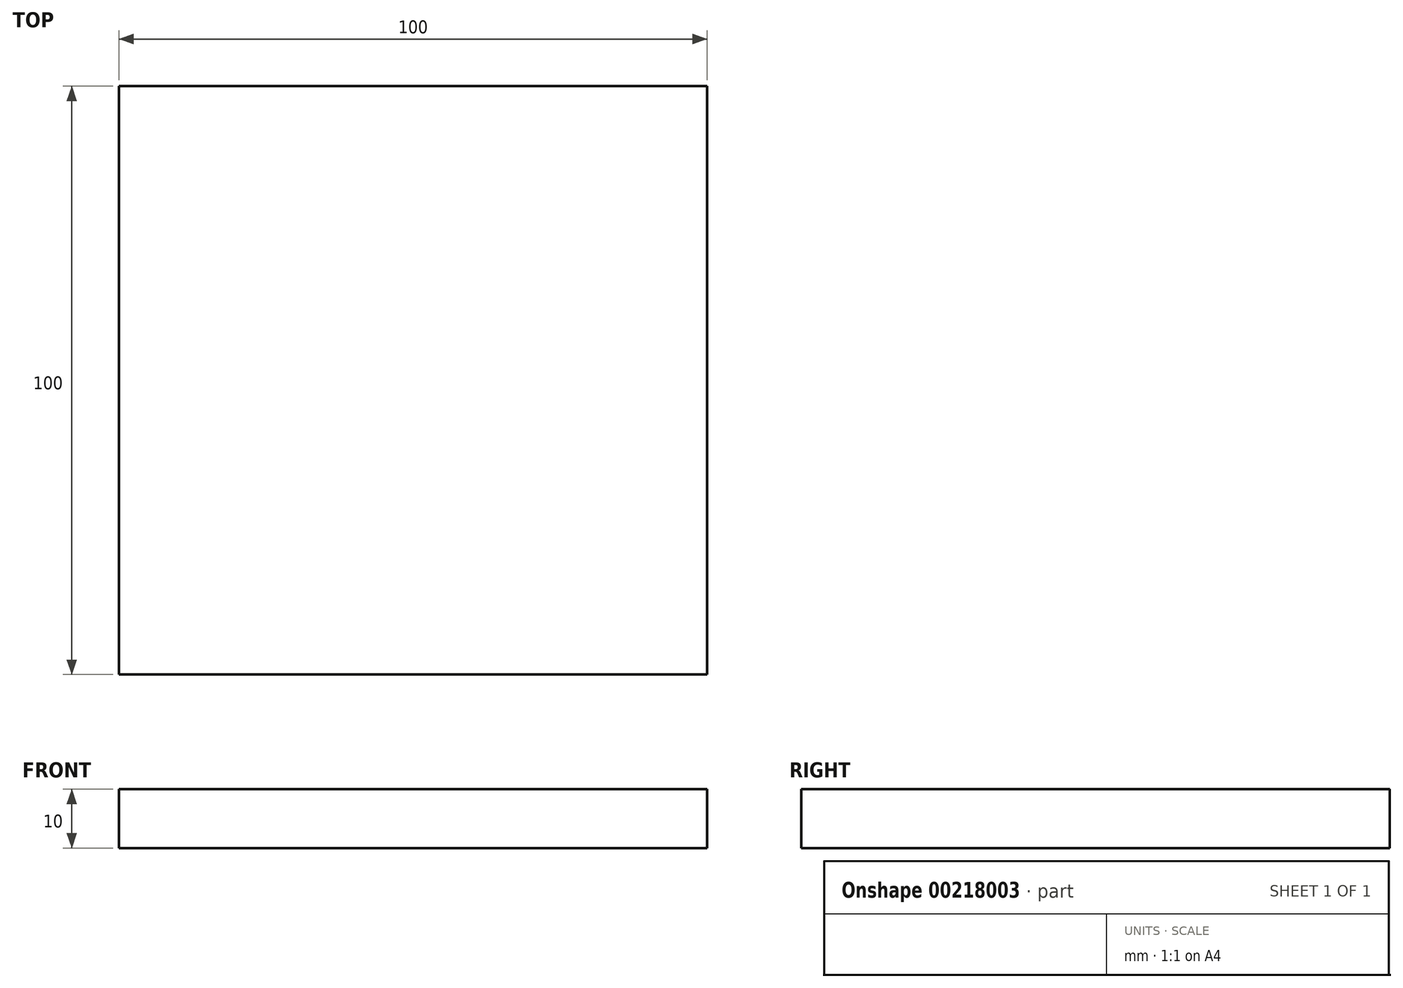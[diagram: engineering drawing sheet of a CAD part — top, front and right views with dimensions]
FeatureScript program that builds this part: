
annotation { "Feature Type Name" : "Feature", "Feature Type Description" : "" }
export const myFeature = defineFeature(function(context is Context, id is Id, definition is map)
    precondition{}
    {
        {
            var Q0;
            Q0=qCreatedBy(makeId("Top.planeOp"),FACE);
            var sketch = newSketch(context, id + "F0", { "sketchPlane" : qUnion([Q0])});
            skLineSegment(sketch, "E0.bottom", {"start": v(-50, 50) * mm, "end": v(50, 50) * mm});
            skLineSegment(sketch, "E0.top", {"start": v(-50, -50) * mm, "end": v(50, -50) * mm});
            skLineSegment(sketch, "E0.left", {"start": v(-50, 50) * mm, "end": v(-50, -50) * mm});
            skLineSegment(sketch, "E0.right", {"start": v(50, 50) * mm, "end": v(50, -50) * mm});
            skPoint(sketch, "E0.middle", {"position": v(0, 0) * mm});
            skSolve(sketch);
        }
        {
            var Q0;
            Q0=makeQuery(id+"F0.imprint","IMPRINT",FACE,{"disambiguationData":[TD([[makeQuery(id+"F0.imprint","IMPRINT",EDGE,{"derivedFrom":sQuery(id+"F0.wireOp",EDGE,"E0.bottom")}),-1.0]])]});
            extrude(context, id + "F1", {"entities" : qUnion([Q0]), "depth" : 10 * mm});
        }
        {
            var Q0;
            Q0=makeQuery(id+"F1.opExtrude","CAP_FACE",FACE,{"disambiguationData":[OSD([sQuery(id+"F0.wireOp",EDGE,"E0.bottom"),sQuery(id+"F0.wireOp",EDGE,"E0.top"),sQuery(id+"F0.wireOp",EDGE,"E0.left"),sQuery(id+"F0.wireOp",EDGE,"E0.right")])],"isStart":false});
            var sketch = newSketch(context, id + "F2", { "sketchPlane" : qUnion([Q0])});
            skCircle(sketch, "E1.cCircle", {"center": v(0, 0) * mm, "radius": 17.5 * mm, "construction": true});
            skLineSegment(sketch, "E1.0", {"start": v(-17.5, -7.25) * mm, "end": v(-17.5, 7.25) * mm});
            skLineSegment(sketch, "E1.1", {"start": v(-17.5, 7.25) * mm, "end": v(-7.25, 17.5) * mm});
            skLineSegment(sketch, "E1.2", {"start": v(-7.25, 17.5) * mm, "end": v(7.25, 17.5) * mm});
            skLineSegment(sketch, "E1.3", {"start": v(7.25, 17.5) * mm, "end": v(17.5, 7.25) * mm});
            skLineSegment(sketch, "E1.4", {"start": v(17.5, 7.25) * mm, "end": v(17.5, -7.25) * mm});
            skLineSegment(sketch, "E1.5", {"start": v(17.5, -7.25) * mm, "end": v(7.25, -17.5) * mm});
            skLineSegment(sketch, "E1.6", {"start": v(7.25, -17.5) * mm, "end": v(-7.25, -17.5) * mm});
            skLineSegment(sketch, "E1.7", {"start": v(-7.25, -17.5) * mm, "end": v(-17.5, -7.25) * mm});
            skPoint(sketch, "E1.0.midPoint", {"position": v(-17.5, 0) * mm});
            skSolve(sketch);
        }
        {
            var Q0;
            Q0=makeQuery(id+"F2.imprint","IMPRINT",FACE,{"disambiguationData":[TD([[makeQuery(id+"F2.imprint","IMPRINT",EDGE,{"derivedFrom":sQuery(id+"F2.wireOp",EDGE,"E1.0")}),-1.0]])]});
            extrude(context, id + "F3", {"entities" : qUnion([Q0]), "operationType" : NewBodyOperationType.ADD, "depth" : 10 * mm});
        }
        {
            var Q0;
            Q0=makeQuery(id+"F3.opExtrude","CAP_FACE",FACE,{"disambiguationData":[OSD([sQuery(id+"F2.wireOp",EDGE,"E1.0"),sQuery(id+"F2.wireOp",EDGE,"E1.1"),sQuery(id+"F2.wireOp",EDGE,"E1.2"),sQuery(id+"F2.wireOp",EDGE,"E1.3"),sQuery(id+"F2.wireOp",EDGE,"E1.4"),sQuery(id+"F2.wireOp",EDGE,"E1.5"),sQuery(id+"F2.wireOp",EDGE,"E1.6"),sQuery(id+"F2.wireOp",EDGE,"E1.7")])],"isStart":false});
            extrude(context, id + "F4", {"entities" : qUnion([Q0]), "operationType" : NewBodyOperationType.REMOVE, "oppositeDirection" : true, "depth" : 10 * mm});
        }
    });
